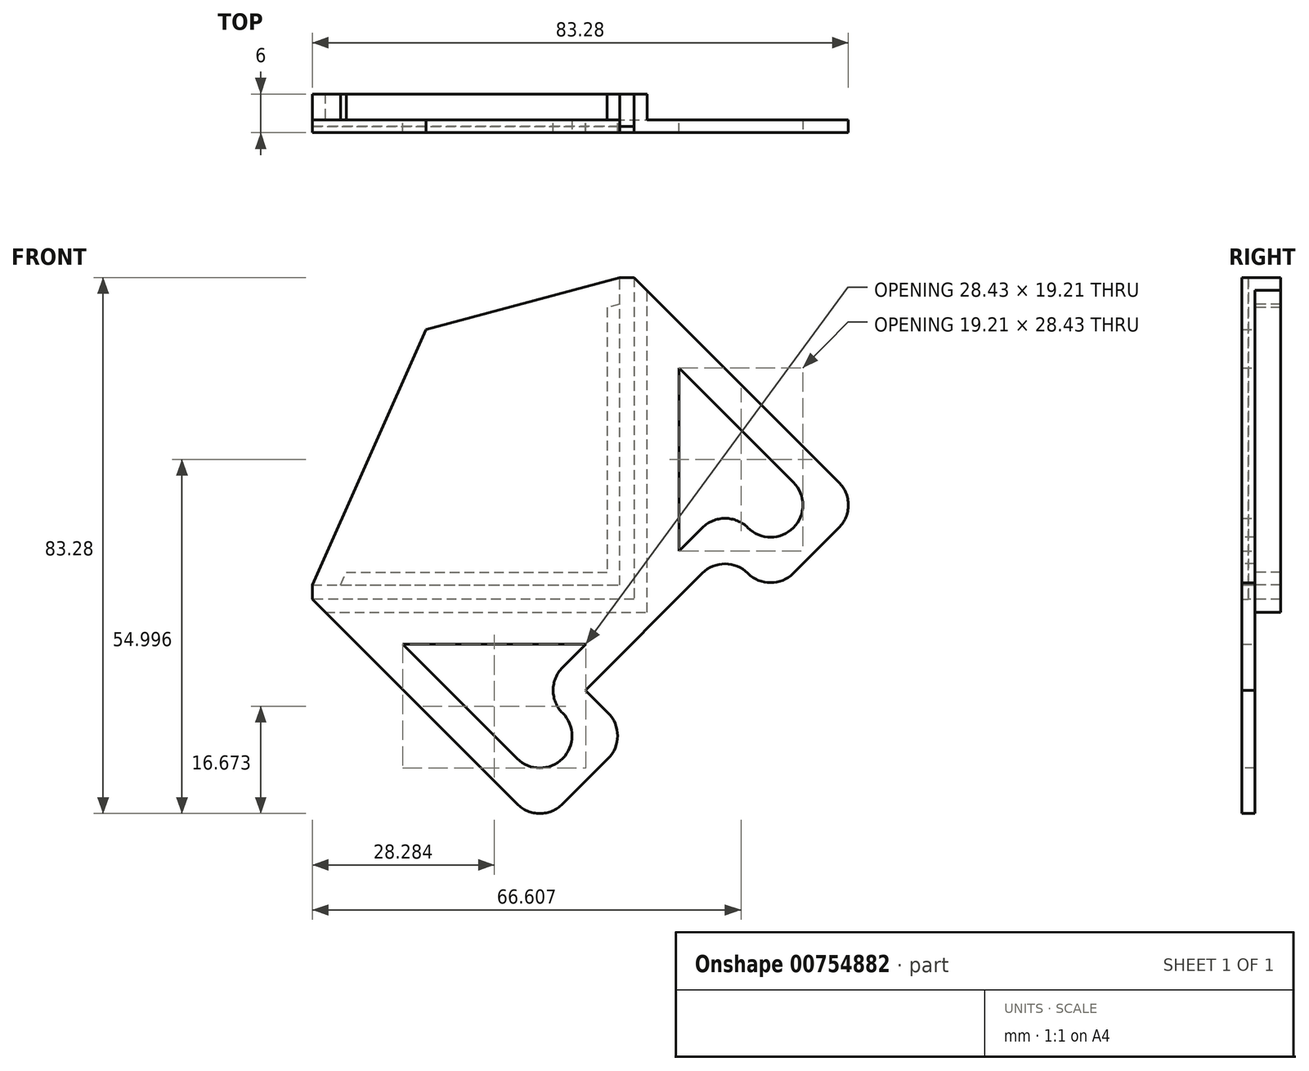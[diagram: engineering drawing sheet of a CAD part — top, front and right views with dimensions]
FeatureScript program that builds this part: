
annotation { "Feature Type Name" : "Feature", "Feature Type Description" : "" }
export const myFeature = defineFeature(function(context is Context, id is Id, definition is map)
    precondition{}
    {
        {
            var Q0;
            Q0=qCreatedBy(makeId("Front.planeOp"),FACE);
            var sketch = newSketch(context, id + "F0", { "sketchPlane" : qUnion([Q0])});
            skLineSegment(sketch, "E0", {"start": v(-50, 0) * mm, "end": v(-50, 2.2) * mm});
            skLineSegment(sketch, "E1", {"start": v(-2.2, 50) * mm, "end": v(0, 50) * mm});
            skLineSegment(sketch, "E2", {"start": v(-2.2, 50) * mm, "end": v(-32.31, 41.93) * mm});
            skLineSegment(sketch, "E3", {"start": v(-32.31, 41.93) * mm, "end": v(-50, 2.2) * mm});
            skLineSegment(sketch, "E4", {"start": v(0, 50) * mm, "end": v(35.36, 14.64) * mm});
            skLineSegment(sketch, "E5", {"start": v(-50, 0) * mm, "end": v(-14.64, -35.36) * mm});
            skLineSegment(sketch, "E6", {"start": v(-14.64, -35.36) * mm, "end": v(-0.5, -21.21) * mm});
            skLineSegment(sketch, "E7", {"start": v(35.36, 14.64) * mm, "end": v(21.21, 0.5) * mm});
            skLineSegment(sketch, "E8", {"start": v(-0.5, -21.21) * mm, "end": v(-7.57, -14.14) * mm});
            skLineSegment(sketch, "E9", {"start": v(-7.57, -14.14) * mm, "end": v(14.14, 7.57) * mm});
            skLineSegment(sketch, "E10", {"start": v(14.14, 7.57) * mm, "end": v(21.21, 0.5) * mm});
            skLineSegment(sketch, "E11", {"start": v(-2.2, 50) * mm, "end": v(-2.2, 2) * mm});
            skLineSegment(sketch, "E12", {"start": v(-50, 2.2) * mm, "end": v(-2, 2.2) * mm});
            skSolve(sketch);
        }
        {
            var Q0;
            Q0 = qSketchRegion(id + "F0", true);
            extrude(context, id + "F1", {"entities" : qUnion([Q0]), "depth" : 2 * mm, "offsetDistance" : 25 * mm});
        }
        {
            var Q0;
            Q0=makeQuery(id+"F1.opExtrude","CAP_FACE",FACE,{"disambiguationData":[OSD([sQuery(id+"F0.wireOp",EDGE,"E0"),sQuery(id+"F0.wireOp",EDGE,"E1"),sQuery(id+"F0.wireOp",EDGE,"E2"),sQuery(id+"F0.wireOp",EDGE,"E3"),sQuery(id+"F0.wireOp",EDGE,"E4"),sQuery(id+"F0.wireOp",EDGE,"E5"),sQuery(id+"F0.wireOp",EDGE,"E6"),sQuery(id+"F0.wireOp",EDGE,"E7"),sQuery(id+"F0.wireOp",EDGE,"E8"),sQuery(id+"F0.wireOp",EDGE,"E9"),sQuery(id+"F0.wireOp",EDGE,"E10")])],"isStart":true});
            var sketch = newSketch(context, id + "F2", { "sketchPlane" : qUnion([Q0])});
            skLineSegment(sketch, "E13", {"start": v(0, 50) * mm, "end": v(0, 0) * mm});
            skLineSegment(sketch, "E14", {"start": v(0, 0) * mm, "end": v(50, 0) * mm});
            skLineSegment(sketch, "E15", {"start": v(50, 0) * mm, "end": v(48, -2) * mm});
            skLineSegment(sketch, "E16", {"start": v(48, -2) * mm, "end": v(-2, -2) * mm});
            skLineSegment(sketch, "E17", {"start": v(-2, -2) * mm, "end": v(-2, 48) * mm});
            skLineSegment(sketch, "E18", {"start": v(-2, 48) * mm, "end": v(0, 50) * mm});
            skLineSegment(sketch, "E19", {"start": v(2.2, 45.86) * mm, "end": v(4.2, 45.32) * mm});
            skLineSegment(sketch, "E20", {"start": v(4.2, 45.32) * mm, "end": v(4.2, 4.2) * mm});
            skLineSegment(sketch, "E21", {"start": v(45.62, 2.2) * mm, "end": v(2.2, 2.2) * mm});
            skLineSegment(sketch, "E22", {"start": v(2.2, 2.2) * mm, "end": v(2.2, 45.86) * mm});
            skLineSegment(sketch, "E23", {"start": v(45.62, 2.2) * mm, "end": v(44.73, 4.2) * mm});
            skLineSegment(sketch, "E24", {"start": v(44.73, 4.2) * mm, "end": v(4.2, 4.2) * mm});
            skSolve(sketch);
        }
        {
            var Q0;
            Q0 = qSketchRegion(id + "F2", true);
            extrude(context, id + "F3", {"entities" : qUnion([Q0]), "operationType" : NewBodyOperationType.ADD, "depth" : 4 * mm, "offsetDistance" : 25 * mm});
        }
        {
            var Q0;
            {var subQ0=sQuery(id+"F0.wireOp",EDGE,"E6");var subQ1=sQuery(id+"F0.wireOp",EDGE,"E10");var subQ2=sQuery(id+"F0.wireOp",EDGE,"E9");var subQ3=sQuery(id+"F0.wireOp",EDGE,"E8");var subQ4=sQuery(id+"F0.wireOp",EDGE,"E7");var subQ5=sQuery(id+"F0.wireOp",EDGE,"E4");var subQ6=sQuery(id+"F0.wireOp",EDGE,"E5");Q0=makeQuery(id+"F3.boolean.opBoolean","SPLIT",FACE,{"disambiguationData":[TD([makeQuery(id+"F1.opExtrude","SWEPT_FACE",FACE,{"disambiguationData":[OSD([subQ0])]})])],"derivedFrom":makeQuery(id+"F1.opExtrude","CAP_FACE",FACE,{"disambiguationData":[OSD([sQuery(id+"F0.wireOp",EDGE,"E0"),sQuery(id+"F0.wireOp",EDGE,"E1"),sQuery(id+"F0.wireOp",EDGE,"E2"),sQuery(id+"F0.wireOp",EDGE,"E3"),subQ5,subQ6,subQ0,subQ4,subQ3,subQ2,subQ1])],"isStart":true})});}
            var sketch = newSketch(context, id + "F4", { "sketchPlane" : qUnion([Q0])});
            skLineSegment(sketch, "E25.0", {"start": v(14.64, -28.28) * mm, "end": v(35.93, -7) * mm});
            skLineSegment(sketch, "E25.1", {"start": v(7.57, -21.21) * mm, "end": v(14.64, -28.28) * mm});
            skLineSegment(sketch, "E25.2", {"start": v(35.93, -7) * mm, "end": v(7.5, -7) * mm});
            skLineSegment(sketch, "E25.3", {"start": v(14.64, -14.14) * mm, "end": v(7.57, -21.21) * mm});
            skLineSegment(sketch, "E25.4", {"start": v(7.5, -7) * mm, "end": v(14.64, -14.14) * mm});
            skLineSegment(sketch, "E25.5", {"start": v(-7, 7.5) * mm, "end": v(-7, 35.93) * mm});
            skLineSegment(sketch, "E25.6", {"start": v(-14.14, 14.64) * mm, "end": v(-7, 7.5) * mm});
            skLineSegment(sketch, "E25.7", {"start": v(-7, 35.93) * mm, "end": v(-28.28, 14.64) * mm});
            skLineSegment(sketch, "E25.8", {"start": v(-28.28, 14.64) * mm, "end": v(-21.21, 7.57) * mm});
            skLineSegment(sketch, "E25.9", {"start": v(-21.21, 7.57) * mm, "end": v(-14.14, 14.64) * mm});
            skSolve(sketch);
        }
        {
            var Q0;
            Q0 = qSketchRegion(id + "F4", true);
            extrude(context, id + "F5", {"entities" : qUnion([Q0]), "operationType" : NewBodyOperationType.REMOVE, "oppositeDirection" : true, "depth" : 25 * mm, "offsetDistance" : 25 * mm});
        }
        {
            var Q0;
            Q0=makeQuery(id+"F1.opExtrude","SWEPT_EDGE",EDGE,{"disambiguationData":[OSD([sQuery(id+"F0.wireOp",EDGE,"E4"),sQuery(id+"F0.wireOp",EDGE,"E7")])]});
            var Q1;
            Q1=makeQuery(id+"F1.opExtrude","SWEPT_EDGE",EDGE,{"disambiguationData":[OSD([sQuery(id+"F0.wireOp",EDGE,"E7"),sQuery(id+"F0.wireOp",EDGE,"E10")])]});
            var Q2;
            Q2=makeQuery(id+"F1.opExtrude","SWEPT_EDGE",EDGE,{"disambiguationData":[OSD([sQuery(id+"F0.wireOp",EDGE,"E5"),sQuery(id+"F0.wireOp",EDGE,"E6")])]});
            var Q3;
            Q3=makeQuery(id+"F1.opExtrude","SWEPT_EDGE",EDGE,{"disambiguationData":[OSD([sQuery(id+"F0.wireOp",EDGE,"E6"),sQuery(id+"F0.wireOp",EDGE,"E8")])]});
            var Q4;
            Q4=makeQuery(id+"F5.boolean.opBoolean","COPY",EDGE,{"derivedFrom":makeQuery(id+"F5.opExtrude","SWEPT_EDGE",EDGE,{"disambiguationData":[OSD([sQuery(id+"F4.wireOp",EDGE,"E25.3"),sQuery(id+"F4.wireOp",EDGE,"E25.4")])]})});
            var Q5;
            Q5=makeQuery(id+"F5.boolean.opBoolean","COPY",EDGE,{"derivedFrom":makeQuery(id+"F5.opExtrude","SWEPT_EDGE",EDGE,{"disambiguationData":[OSD([sQuery(id+"F4.wireOp",EDGE,"E25.6"),sQuery(id+"F4.wireOp",EDGE,"E25.9")])]})});
            var Q6;
            Q6=makeQuery(id+"F1.opExtrude","SWEPT_EDGE",EDGE,{"disambiguationData":[OSD([sQuery(id+"F0.wireOp",EDGE,"E9"),sQuery(id+"F0.wireOp",EDGE,"E10")])]});
            var Q7;
            Q7=makeQuery(id+"F5.boolean.opBoolean","COPY",EDGE,{"derivedFrom":makeQuery(id+"F5.opExtrude","SWEPT_EDGE",EDGE,{"disambiguationData":[OSD([sQuery(id+"F4.wireOp",EDGE,"E25.8"),sQuery(id+"F4.wireOp",EDGE,"E25.9")])]})});
            var Q8;
            Q8=makeQuery(id+"F5.boolean.opBoolean","COPY",EDGE,{"derivedFrom":makeQuery(id+"F5.opExtrude","SWEPT_EDGE",EDGE,{"disambiguationData":[OSD([sQuery(id+"F4.wireOp",EDGE,"E25.7"),sQuery(id+"F4.wireOp",EDGE,"E25.8")])]})});
            var Q9;
            Q9=makeQuery(id+"F5.boolean.opBoolean","COPY",EDGE,{"derivedFrom":makeQuery(id+"F5.opExtrude","SWEPT_EDGE",EDGE,{"disambiguationData":[OSD([sQuery(id+"F4.wireOp",EDGE,"E25.0"),sQuery(id+"F4.wireOp",EDGE,"E25.1")])]})});
            var Q10;
            Q10=makeQuery(id+"F5.boolean.opBoolean","COPY",EDGE,{"derivedFrom":makeQuery(id+"F5.opExtrude","SWEPT_EDGE",EDGE,{"disambiguationData":[OSD([sQuery(id+"F4.wireOp",EDGE,"E25.1"),sQuery(id+"F4.wireOp",EDGE,"E25.3")])]})});
            fillet(context, id + "F6", {"entities" : qUnion([Q0, Q1, Q2, Q3, Q4, Q5, Q6, Q7, Q8, Q9, Q10]), "radius" : 5 * mm, "tangentPropagation" : true, "allowEdgeOverflow" : false});
        }
        {
            var Q0;
            {var subQ0=sQuery(id+"F0.wireOp",EDGE,"E2");var subQ1=sQuery(id+"F0.wireOp",EDGE,"E5");var subQ2=sQuery(id+"F0.wireOp",EDGE,"E4");var subQ3=sQuery(id+"F0.wireOp",EDGE,"E0");var subQ4=sQuery(id+"F0.wireOp",EDGE,"E3");var subQ5=sQuery(id+"F0.wireOp",EDGE,"E1");Q0=makeQuery(id+"F3.boolean.opBoolean","SPLIT",FACE,{"disambiguationData":[TD([makeQuery(id+"F1.opExtrude","SWEPT_FACE",FACE,{"disambiguationData":[OSD([subQ3])]})])],"derivedFrom":makeQuery(id+"F1.opExtrude","CAP_FACE",FACE,{"disambiguationData":[OSD([subQ3,subQ5,subQ0,subQ4,subQ2,subQ1,sQuery(id+"F0.wireOp",EDGE,"E6"),sQuery(id+"F0.wireOp",EDGE,"E7"),sQuery(id+"F0.wireOp",EDGE,"E8"),sQuery(id+"F0.wireOp",EDGE,"E9"),sQuery(id+"F0.wireOp",EDGE,"E10")])],"isStart":true})});}
            var sketch = newSketch(context, id + "F7", { "sketchPlane" : qUnion([Q0])});
            skLineSegment(sketch, "E26", {"start": v(0, 50) * mm, "end": v(0, 0) * mm});
            skLineSegment(sketch, "E27", {"start": v(0, 0) * mm, "end": v(50, 0) * mm});
            skLineSegment(sketch, "E28", {"start": v(50, 0) * mm, "end": v(50, 2.2) * mm});
            skLineSegment(sketch, "E29", {"start": v(50, 2.2) * mm, "end": v(2.2, 2.2) * mm});
            skLineSegment(sketch, "E30", {"start": v(2.2, 2.2) * mm, "end": v(2.2, 50) * mm});
            skLineSegment(sketch, "E31", {"start": v(2.2, 50) * mm, "end": v(0, 50) * mm});
            skSolve(sketch);
        }
        {
            var Q0;
            Q0=makeQuery(id+"F7.imprint","IMPRINT",FACE,{"disambiguationData":[TD([[makeQuery(id+"F7.imprint","IMPRINT",EDGE,{"derivedFrom":sQuery(id+"F7.wireOp",EDGE,"E26")}),1.0]])]});
            extrude(context, id + "F8", {"entities" : qUnion([Q0]), "operationType" : NewBodyOperationType.REMOVE, "oppositeDirection" : true, "depth" : 1 * mm, "offsetDistance" : 25 * mm});
        }
    });
